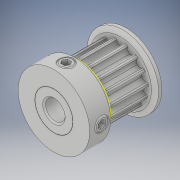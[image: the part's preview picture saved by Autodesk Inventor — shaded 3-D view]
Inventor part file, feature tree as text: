
AUTODESK INVENTOR PART (.ipt)
format: ipt  version: 2019.2 (Build 232265000, 265)  size: 397,312 bytes
history: native  units: mm
features: other x1, sketch x1, imported_body x1
ambient origin geometry x8: Origin, YZ Plane, XZ Plane, XY Plane, X Axis, Y Axis, Z Axis, Center Point
bodies: Solid1 (feature_tree)
feature tree (3):
  other  "gates_P15-3M-09AL.stp"
  sketch  "Sketch1"
  imported_body  "Base1"
